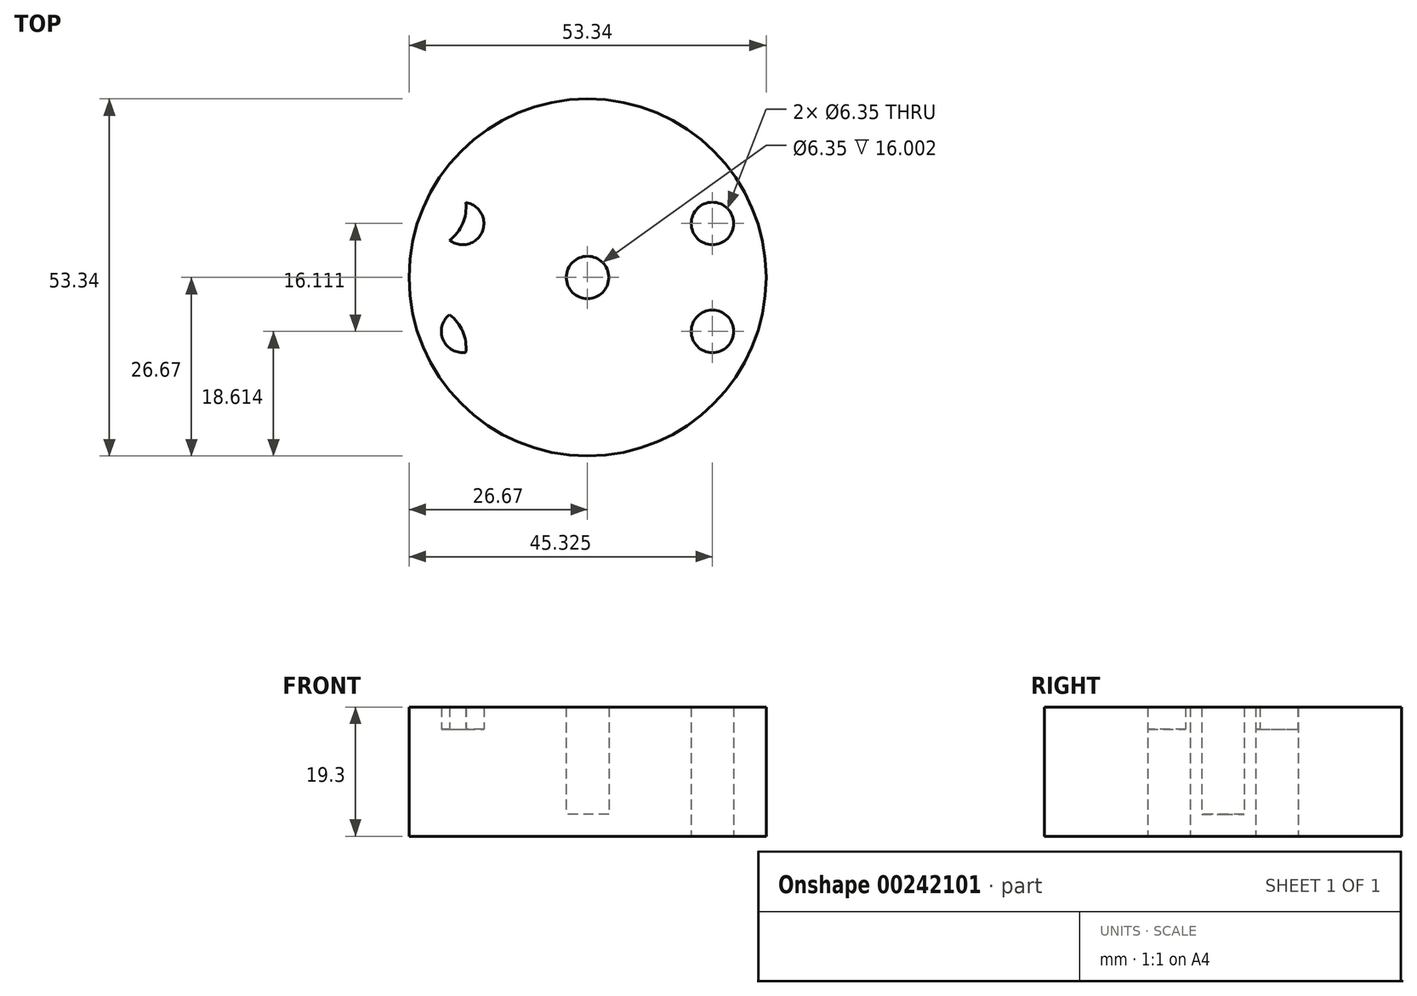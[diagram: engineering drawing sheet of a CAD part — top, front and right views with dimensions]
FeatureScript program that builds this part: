
annotation { "Feature Type Name" : "Feature", "Feature Type Description" : "" }
export const myFeature = defineFeature(function(context is Context, id is Id, definition is map)
    precondition{}
    {
        {
            var Q0;
            Q0=qCreatedBy(makeId("Top.planeOp"),FACE);
            var sketch = newSketch(context, id + "F0", { "sketchPlane" : qUnion([Q0])});
            skCircle(sketch, "E0", {"center": v(0, 0) * mm, "radius": 26.67 * mm});
            skCircle(sketch, "E1", {"center": v(-24.48, 10.57) * mm, "radius": 6.35 * mm});
            skCircle(sketch, "E2", {"center": v(0, 0) * mm, "radius": 3.18 * mm});
            skCircle(sketch, "E3.MirrorC", {"center": v(24.48, 10.57) * mm, "radius": 6.35 * mm});
            skCircle(sketch, "E4.MirrorC", {"center": v(-24.48, -10.57) * mm, "radius": 6.35 * mm});
            skCircle(sketch, "E5.MirrorC", {"center": v(24.48, -10.57) * mm, "radius": 6.35 * mm});
            skCircle(sketch, "E6", {"center": v(-18.65, 8.06) * mm, "radius": 3.18 * mm});
            skCircle(sketch, "E7", {"center": v(18.65, 8.06) * mm, "radius": 3.18 * mm});
            skCircle(sketch, "E8.MirrorC", {"center": v(-18.65, -8.06) * mm, "radius": 3.18 * mm});
            skCircle(sketch, "E9.MirrorC", {"center": v(18.65, -8.06) * mm, "radius": 3.18 * mm});
            skSolve(sketch);
        }
        {
            var Q0;
            Q0=makeQuery(id+"F0.imprint","IMPRINT",FACE,{"disambiguationData":[TD([[makeQuery(id+"F0.imprint","IMPRINT",EDGE,{"derivedFrom":sQuery(id+"F0.wireOp",EDGE,"E2")}),-1.0]])]});
            var Q1;
            Q1=makeQuery(id+"F0.imprint","IMPRINT",FACE,{"disambiguationData":[TD([[makeQuery(id+"F0.imprint","IMPRINT",EDGE,{"derivedFrom":sQuery(id+"F0.wireOp",EDGE,"E2")}),1.0]])]});
            extrude(context, id + "F1", {"entities" : qUnion([Q0, Q1]), "depth" : 3.3 * mm});
        }
        {
            var Q0;
            {var subQ0=sQuery(id+"F0.wireOp",EDGE,"E7");var subQ1=sQuery(id+"F0.wireOp",EDGE,"E3.MirrorC");var subQ2=makeQuery(id+"F0.imprint","INTERSECT",VERTEX,{"disambiguationData":[OD(0.0)],"derivedFrom":[subQ1,subQ0]});Q0=makeQuery(id+"F0.imprint","IMPRINT",FACE,{"disambiguationData":[TD([[makeQuery(id+"F0.imprint","IMPRINT",EDGE,{"disambiguationData":[TD([[subQ2,1.0]])],"derivedFrom":subQ1}),1.0]])]});}
            var Q1;
            {var subQ0=sQuery(id+"F0.wireOp",EDGE,"E9.MirrorC");var subQ1=sQuery(id+"F0.wireOp",EDGE,"E5.MirrorC");var subQ2=makeQuery(id+"F0.imprint","INTERSECT",VERTEX,{"disambiguationData":[OD(0.0)],"derivedFrom":[subQ1,subQ0]});Q1=makeQuery(id+"F0.imprint","IMPRINT",FACE,{"disambiguationData":[TD([[makeQuery(id+"F0.imprint","IMPRINT",EDGE,{"disambiguationData":[TD([[subQ2,1.0]])],"derivedFrom":subQ1}),-1.0]])]});}
            var Q2;
            {var subQ0=sQuery(id+"F0.wireOp",EDGE,"E8.MirrorC");var subQ1=sQuery(id+"F0.wireOp",EDGE,"E4.MirrorC");var subQ2=makeQuery(id+"F0.imprint","INTERSECT",VERTEX,{"disambiguationData":[OD(0.0)],"derivedFrom":[subQ1,subQ0]});Q2=makeQuery(id+"F0.imprint","IMPRINT",FACE,{"disambiguationData":[TD([[makeQuery(id+"F0.imprint","IMPRINT",EDGE,{"disambiguationData":[TD([[subQ2,1.0]])],"derivedFrom":subQ1}),1.0]])]});}
            var Q3;
            {var subQ0=sQuery(id+"F0.wireOp",EDGE,"E6");var subQ1=sQuery(id+"F0.wireOp",EDGE,"E1");var subQ2=makeQuery(id+"F0.imprint","INTERSECT",VERTEX,{"disambiguationData":[OD(0.0)],"derivedFrom":[subQ1,subQ0]});Q3=makeQuery(id+"F0.imprint","IMPRINT",FACE,{"disambiguationData":[TD([[makeQuery(id+"F0.imprint","IMPRINT",EDGE,{"disambiguationData":[TD([[subQ2,1.0]])],"derivedFrom":subQ1}),-1.0]])]});}
            extrude(context, id + "F2", {"entities" : qUnion([Q0, Q1, Q2, Q3]), "operationType" : NewBodyOperationType.ADD, "depth" : 16 * mm});
        }
        {
            var Q0;
            {var subQ0=sQuery(id+"F0.wireOp",EDGE,"E6");var subQ1=sQuery(id+"F0.wireOp",EDGE,"E1");var subQ2=makeQuery(id+"F0.imprint","INTERSECT",VERTEX,{"disambiguationData":[OD(0.0)],"derivedFrom":[subQ1,subQ0]});Q0=makeQuery(id+"F0.imprint","IMPRINT",FACE,{"disambiguationData":[TD([[makeQuery(id+"F0.imprint","IMPRINT",EDGE,{"disambiguationData":[TD([[subQ2,1.0]])],"derivedFrom":subQ1}),1.0]])]});}
            var Q1;
            {var subQ0=sQuery(id+"F0.wireOp",EDGE,"E1");var subQ1=sQuery(id+"F0.wireOp",EDGE,"E0");var subQ2=makeQuery(id+"F0.imprint","INTERSECT",VERTEX,{"disambiguationData":[OD(0.0)],"derivedFrom":[subQ1,subQ0]});Q1=makeQuery(id+"F0.imprint","IMPRINT",FACE,{"disambiguationData":[TD([[makeQuery(id+"F0.imprint","IMPRINT",EDGE,{"disambiguationData":[TD([[subQ2,-1.0]])],"derivedFrom":subQ1}),1.0]])]});}
            var Q2;
            {var subQ0=sQuery(id+"F0.wireOp",EDGE,"E8.MirrorC");var subQ1=sQuery(id+"F0.wireOp",EDGE,"E4.MirrorC");var subQ2=makeQuery(id+"F0.imprint","INTERSECT",VERTEX,{"disambiguationData":[OD(0.0)],"derivedFrom":[subQ1,subQ0]});Q2=makeQuery(id+"F0.imprint","IMPRINT",FACE,{"disambiguationData":[TD([[makeQuery(id+"F0.imprint","IMPRINT",EDGE,{"disambiguationData":[TD([[subQ2,1.0]])],"derivedFrom":subQ1}),-1.0]])]});}
            var Q3;
            {var subQ0=sQuery(id+"F0.wireOp",EDGE,"E4.MirrorC");var subQ1=sQuery(id+"F0.wireOp",EDGE,"E0");var subQ2=makeQuery(id+"F0.imprint","INTERSECT",VERTEX,{"disambiguationData":[OD(0.0)],"derivedFrom":[subQ1,subQ0]});Q3=makeQuery(id+"F0.imprint","IMPRINT",FACE,{"disambiguationData":[TD([[makeQuery(id+"F0.imprint","IMPRINT",EDGE,{"disambiguationData":[TD([[subQ2,-1.0]])],"derivedFrom":subQ1}),1.0]])]});}
            var Q4;
            {var subQ0=sQuery(id+"F0.wireOp",EDGE,"E7");var subQ1=sQuery(id+"F0.wireOp",EDGE,"E3.MirrorC");var subQ2=makeQuery(id+"F0.imprint","INTERSECT",VERTEX,{"disambiguationData":[OD(0.0)],"derivedFrom":[subQ1,subQ0]});Q4=makeQuery(id+"F0.imprint","IMPRINT",FACE,{"disambiguationData":[TD([[makeQuery(id+"F0.imprint","IMPRINT",EDGE,{"disambiguationData":[TD([[subQ2,1.0]])],"derivedFrom":subQ1}),-1.0]])]});}
            var Q5;
            {var subQ0=sQuery(id+"F0.wireOp",EDGE,"E3.MirrorC");var subQ1=sQuery(id+"F0.wireOp",EDGE,"E0");var subQ2=makeQuery(id+"F0.imprint","INTERSECT",VERTEX,{"disambiguationData":[OD(0.0)],"derivedFrom":[subQ1,subQ0]});Q5=makeQuery(id+"F0.imprint","IMPRINT",FACE,{"disambiguationData":[TD([[makeQuery(id+"F0.imprint","IMPRINT",EDGE,{"disambiguationData":[TD([[subQ2,1.0]])],"derivedFrom":subQ1}),1.0]])]});}
            var Q6;
            {var subQ0=sQuery(id+"F0.wireOp",EDGE,"E9.MirrorC");var subQ1=sQuery(id+"F0.wireOp",EDGE,"E5.MirrorC");var subQ2=makeQuery(id+"F0.imprint","INTERSECT",VERTEX,{"disambiguationData":[OD(0.0)],"derivedFrom":[subQ1,subQ0]});Q6=makeQuery(id+"F0.imprint","IMPRINT",FACE,{"disambiguationData":[TD([[makeQuery(id+"F0.imprint","IMPRINT",EDGE,{"disambiguationData":[TD([[subQ2,1.0]])],"derivedFrom":subQ1}),1.0]])]});}
            var Q7;
            {var subQ0=sQuery(id+"F0.wireOp",EDGE,"E5.MirrorC");var subQ1=sQuery(id+"F0.wireOp",EDGE,"E0");var subQ2=makeQuery(id+"F0.imprint","INTERSECT",VERTEX,{"disambiguationData":[OD(0.0)],"derivedFrom":[subQ1,subQ0]});Q7=makeQuery(id+"F0.imprint","IMPRINT",FACE,{"disambiguationData":[TD([[makeQuery(id+"F0.imprint","IMPRINT",EDGE,{"disambiguationData":[TD([[subQ2,-1.0]])],"derivedFrom":subQ1}),1.0]])]});}
            extrude(context, id + "F3", {"entities" : qUnion([Q0, Q1, Q2, Q3, Q4, Q5, Q6, Q7]), "operationType" : NewBodyOperationType.ADD, "depth" : 19.3 * mm});
        }
    });
